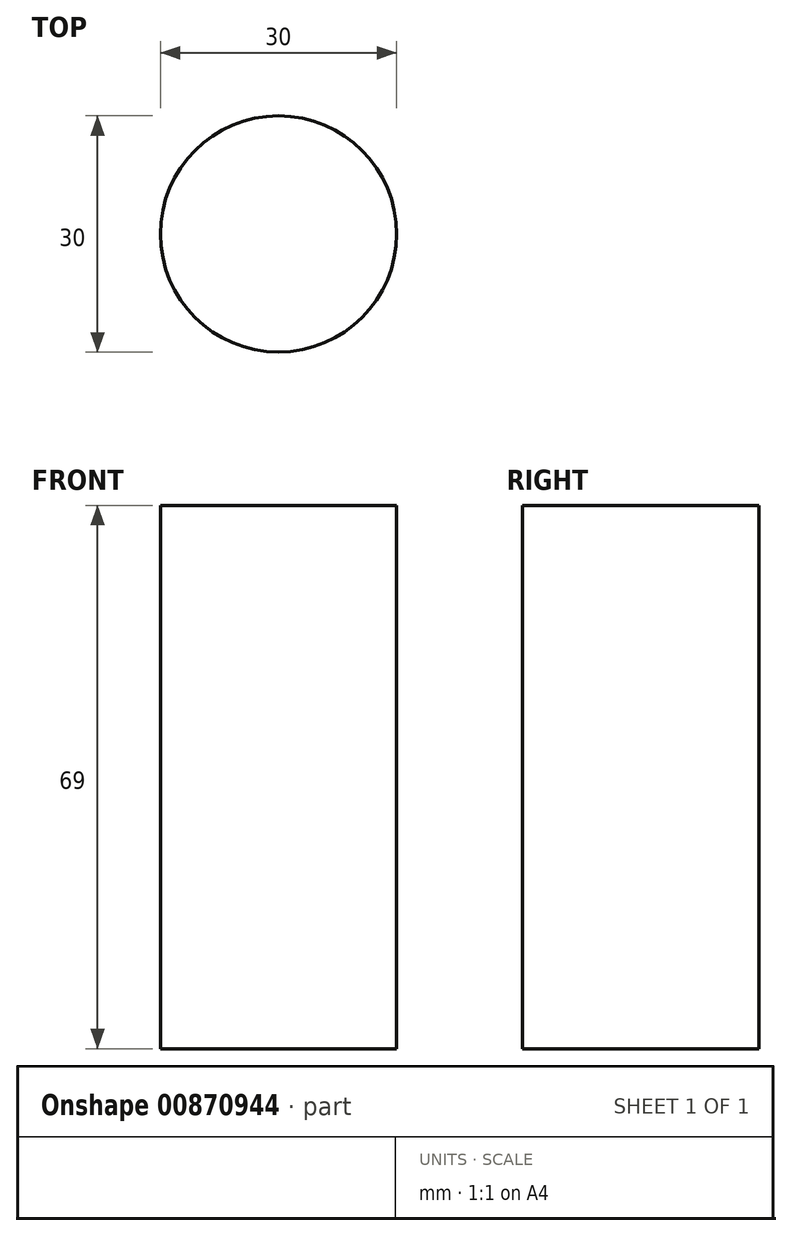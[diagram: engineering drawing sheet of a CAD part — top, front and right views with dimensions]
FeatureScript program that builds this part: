
annotation { "Feature Type Name" : "Feature", "Feature Type Description" : "" }
export const myFeature = defineFeature(function(context is Context, id is Id, definition is map)
    precondition{}
    {
        {
            var Q0;
            Q0=qCreatedBy(makeId("Top.planeOp"),FACE);
            var sketch = newSketch(context, id + "F0", { "sketchPlane" : qUnion([Q0])});
            skCircle(sketch, "E0", {"center": v(0, 0) * mm, "radius": 15 * mm});
            skSolve(sketch);
        }
        {
            var Q0;
            Q0=makeQuery(id+"F0.imprint","IMPRINT",FACE,{"disambiguationData":[TD([[makeQuery(id+"F0.imprint","IMPRINT",EDGE,{"derivedFrom":sQuery(id+"F0.wireOp",EDGE,"E0")}),1.0]])]});
            extrude(context, id + "F1", {"entities" : qUnion([Q0]), "depth" : 39 * mm, "offsetDistance" : 25 * mm, "hasSecondDirection" : true, "secondDirectionOppositeDirection" : true, "secondDirectionDepth" : 30 * mm});
        }
    });
